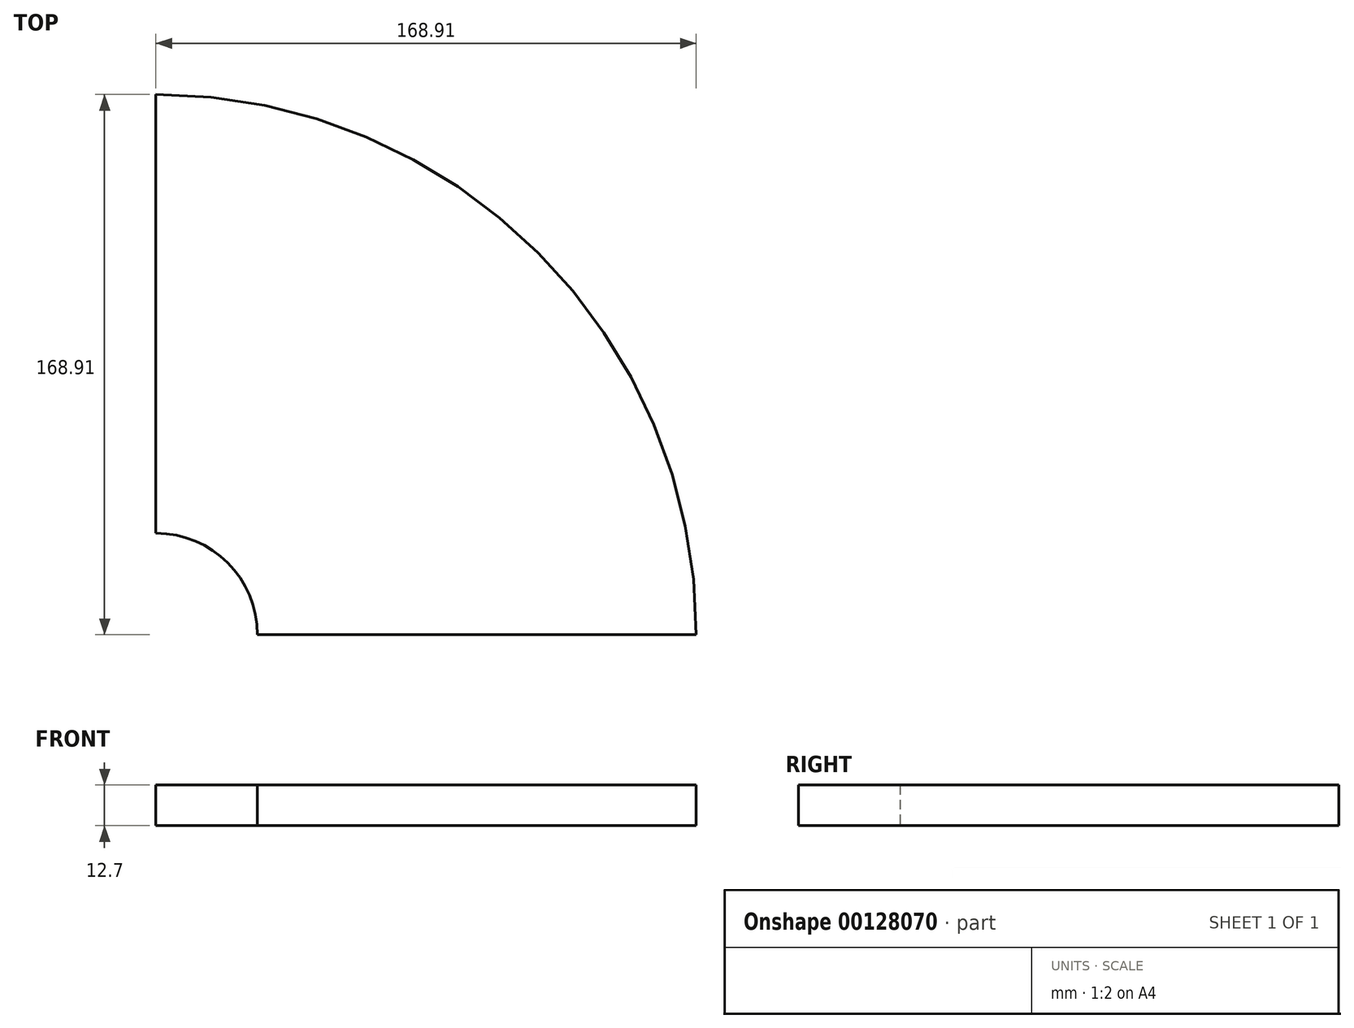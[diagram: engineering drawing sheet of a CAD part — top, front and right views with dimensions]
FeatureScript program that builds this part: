
annotation { "Feature Type Name" : "Feature", "Feature Type Description" : "" }
export const myFeature = defineFeature(function(context is Context, id is Id, definition is map)
    precondition{}
    {
        {
            var Q0;
            Q0=qCreatedBy(makeId("Top.planeOp"),FACE);
            var sketch = newSketch(context, id + "F0", { "sketchPlane" : qUnion([Q0])});
            skArc(sketch, "E0", {"start": v(31.75, 0) * mm, "mid": v(22.45, 22.45) * mm, "end": v(0, 31.75) * mm});
            skArc(sketch, "E1", {"start": v(168.91, 0) * mm, "mid": v(119.44, 119.44) * mm, "end": v(0, 168.91) * mm});
            skLineSegment(sketch, "E2", {"start": v(31.75, 0) * mm, "end": v(168.91, 0) * mm});
            skLineSegment(sketch, "E3", {"start": v(0, 31.75) * mm, "end": v(0, 168.91) * mm});
            skSolve(sketch);
        }
        {
            var Q0;
            Q0=makeQuery(id+"F0.imprint","IMPRINT",FACE,{"disambiguationData":[TD([[makeQuery(id+"F0.imprint","IMPRINT",EDGE,{"derivedFrom":sQuery(id+"F0.wireOp",EDGE,"E0")}),-1.0]])]});
            extrude(context, id + "F1", {"entities" : qUnion([Q0]), "depth" : 12.7 * mm});
        }
    });
